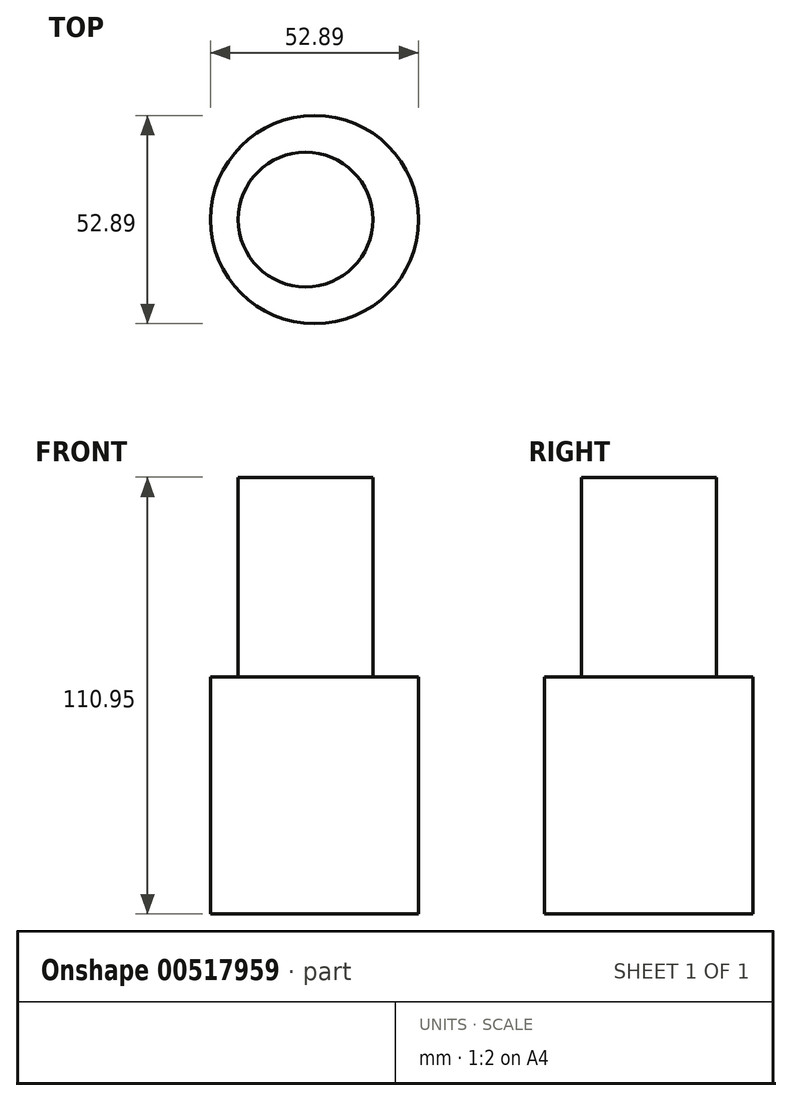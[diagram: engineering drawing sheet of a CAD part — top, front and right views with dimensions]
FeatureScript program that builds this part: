
annotation { "Feature Type Name" : "Feature", "Feature Type Description" : "" }
export const myFeature = defineFeature(function(context is Context, id is Id, definition is map)
    precondition{}
    {
        {
            var Q0;
            Q0=qCreatedBy(makeId("Top.planeOp"),FACE);
            var sketch = newSketch(context, id + "F0", { "sketchPlane" : qUnion([Q0])});
            skCircle(sketch, "E0", {"center": v(-31.5, 22.2) * mm, "radius": 26.44 * mm});
            skSolve(sketch);
        }
        {
            var Q0;
            Q0 = qSketchRegion(id + "F0", true);
            extrude(context, id + "F1", {"entities" : qUnion([Q0]), "depth" : 5.18 * mm, "offsetDistance" : 25.4 * mm});
        }
        {
            var Q0;
            Q0=makeQuery(id+"F1.opExtrude","CAP_FACE",FACE,{"disambiguationData":[OSD([sQuery(id+"F0.wireOp",EDGE,"E0")])],"isStart":false});
            extrude(context, id + "F2", {"entities" : qUnion([Q0]), "operationType" : NewBodyOperationType.ADD, "depth" : 55.08 * mm, "offsetDistance" : 25.4 * mm});
        }
        {
            var Q0;
            Q0=qCreatedBy(makeId("Top.planeOp"),FACE);
            var sketch = newSketch(context, id + "F3", { "sketchPlane" : qUnion([Q0])});
            skCircle(sketch, "E1", {"center": v(-33.8, 22.23) * mm, "radius": 17.12 * mm});
            skSolve(sketch);
        }
        {
            var Q0;
            Q0=makeQuery(id+"F3.imprint","IMPRINT",FACE,{"disambiguationData":[TD([[makeQuery(id+"F3.imprint","IMPRINT",EDGE,{"derivedFrom":sQuery(id+"F3.wireOp",EDGE,"E1")}),1.0]])]});
            var Q1;
            Q1 = qSketchRegion(id + "F3", true);
            extrude(context, id + "F4", {"entities" : qUnion([Q0, Q1]), "operationType" : NewBodyOperationType.ADD, "depth" : 110.95 * mm, "offsetDistance" : 25.4 * mm});
        }
    });
